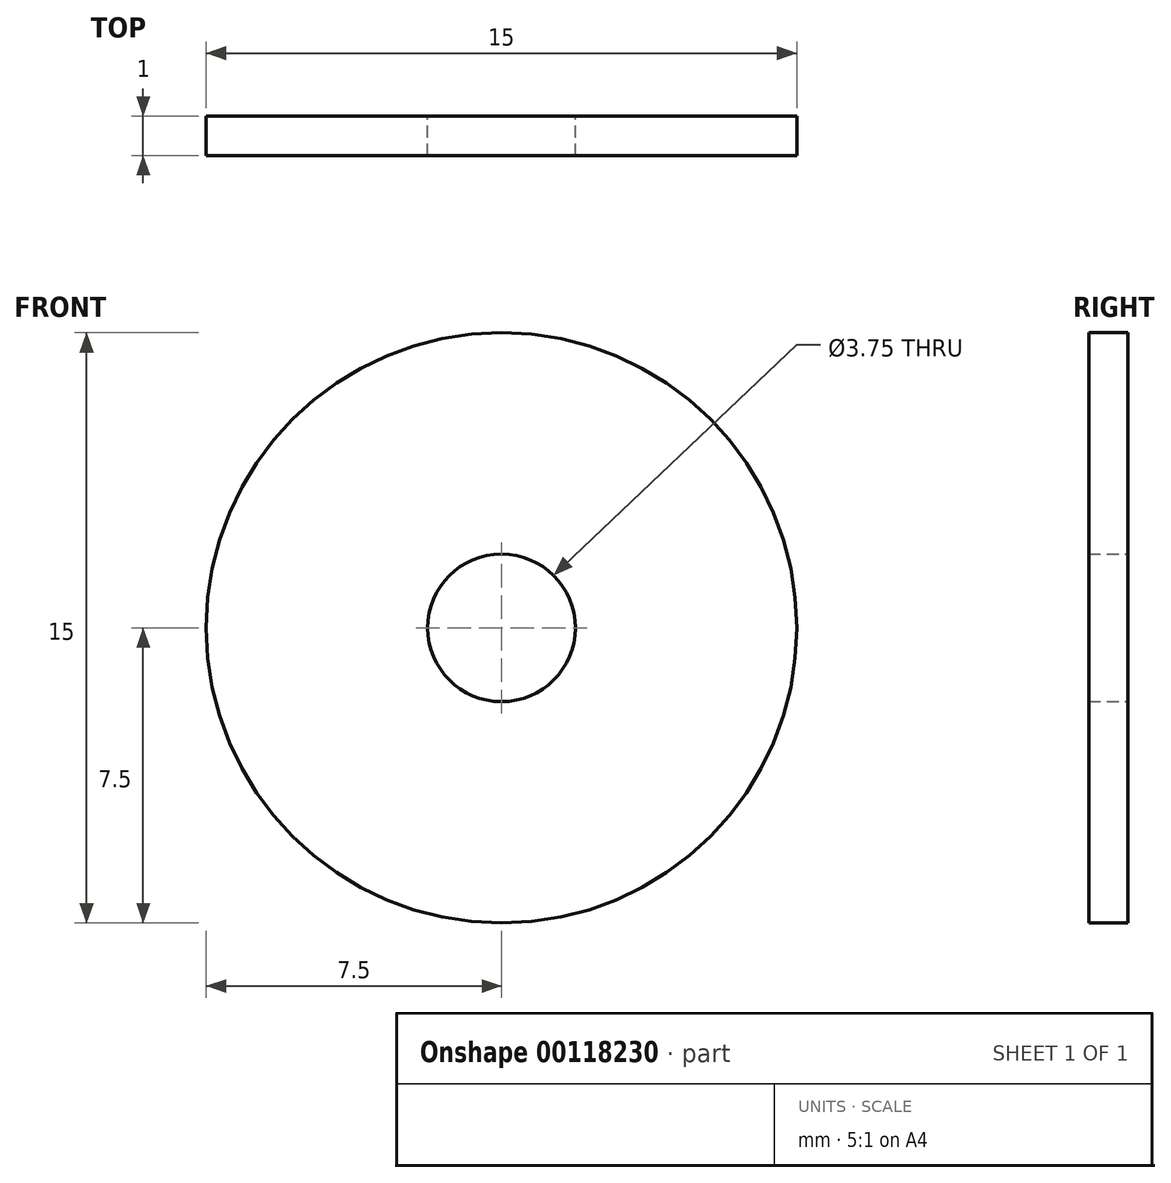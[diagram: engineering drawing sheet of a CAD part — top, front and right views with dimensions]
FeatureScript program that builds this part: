
annotation { "Feature Type Name" : "Feature", "Feature Type Description" : "" }
export const myFeature = defineFeature(function(context is Context, id is Id, definition is map)
    precondition{}
    {
        {
            var Q0;
            Q0=qCreatedBy(makeId("Front.planeOp"),FACE);
            var sketch = newSketch(context, id + "F0", { "sketchPlane" : qUnion([Q0])});
            skCircle(sketch, "E0", {"center": v(0, 0) * mm, "radius": 7.5 * mm});
            skCircle(sketch, "E1", {"center": v(0, 0) * mm, "radius": 1.88 * mm});
            skSolve(sketch);
        }
        {
            var Q0;
            Q0 = qSketchRegion(id + "F0", true);
            extrude(context, id + "F1", {"entities" : qUnion([Q0]), "depth" : 1 * mm});
        }
    });
